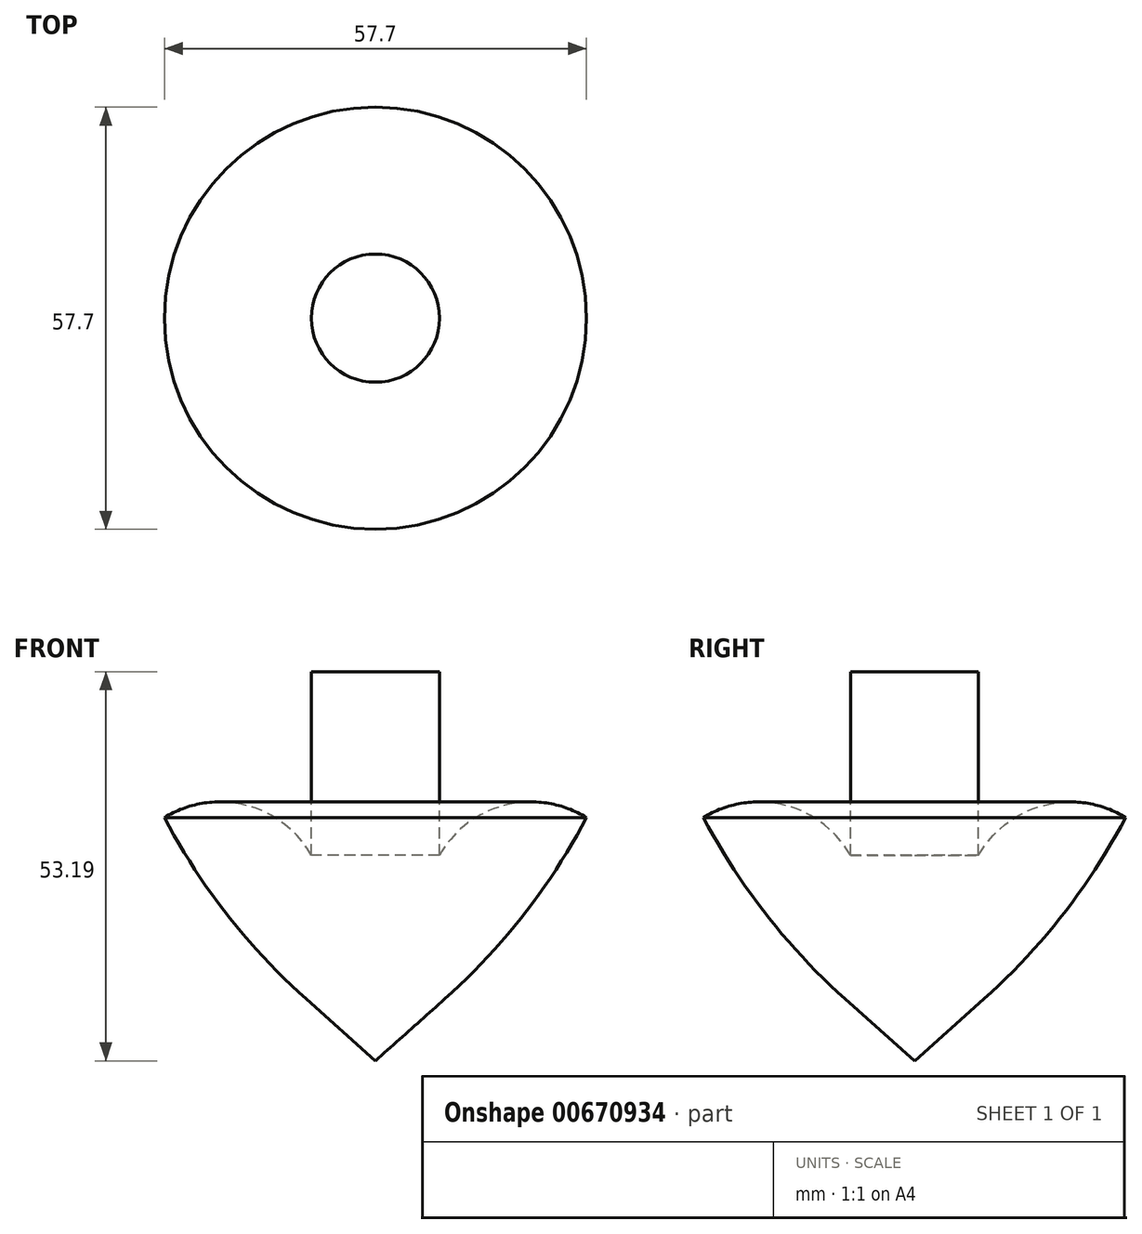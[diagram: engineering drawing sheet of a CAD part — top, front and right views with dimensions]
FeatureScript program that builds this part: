
annotation { "Feature Type Name" : "Feature", "Feature Type Description" : "" }
export const myFeature = defineFeature(function(context is Context, id is Id, definition is map)
    precondition{}
    {
        {
            var Q0;
            Q0=qCreatedBy(makeId("Front.planeOp"),FACE);
            var sketch = newSketch(context, id + "F0", { "sketchPlane" : qUnion([Q0])});
            skLineSegment(sketch, "E0", {"start": v(0, 0) * mm, "end": v(31.75, 0) * mm});
            skLineSegment(sketch, "E1", {"start": v(31.75, 0) * mm, "end": v(31.75, 63.5) * mm});
            skLineSegment(sketch, "E2", {"start": v(0, 0) * mm, "end": v(-31.75, 0) * mm});
            skLineSegment(sketch, "E3", {"start": v(-31.75, 0) * mm, "end": v(-31.75, 63.5) * mm});
            skLineSegment(sketch, "E4", {"start": v(0, 0) * mm, "end": v(9.48, 8.46) * mm});
            skArc(sketch, "E5", {"start": v(9.48, 8.46) * mm, "mid": v(20.28, 20) * mm, "end": v(28.85, 33.28) * mm});
            skArc(sketch, "E6", {"start": v(28.85, 33.28) * mm, "mid": v(17.71, 34.95) * mm, "end": v(8.76, 28.11) * mm});
            skLineSegment(sketch, "E7", {"start": v(8.76, 28.11) * mm, "end": v(8.76, 53.19) * mm});
            skLineSegment(sketch, "E8", {"start": v(8.76, 53.19) * mm, "end": v(0, 53.19) * mm});
            skLineSegment(sketch, "E9", {"start": v(0, 53.19) * mm, "end": v(0, 0) * mm});
            skSolve(sketch);
        }
        {
            var Q0;
            Q0=makeQuery(id+"F0.imprint","IMPRINT",FACE,{"disambiguationData":[TD([[makeQuery(id+"F0.imprint","IMPRINT",EDGE,{"derivedFrom":sQuery(id+"F0.wireOp",EDGE,"E4")}),1.0]])]});
            var Q1;
            Q1=sQuery(id+"F0.wireOp",EDGE,"E9");
            revolve(context, id + "F1", {"entities" : qUnion([Q0]), "axis" : qUnion([Q1]), "revolveType" : RevolveType.FULL});
        }
    });
